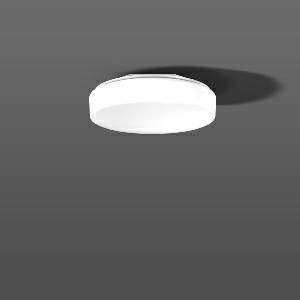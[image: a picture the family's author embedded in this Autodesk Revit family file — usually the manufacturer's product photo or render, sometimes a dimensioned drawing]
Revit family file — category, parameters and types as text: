
# Revit family: flat_polymero_kreis_672092_002_6_1_e46d
name_source: partatom
category: Lighting Fixtures
units: mm (PartAtom-declared; Revit-internal decimal feet)

## family parameters
Cut with Voids When Loaded = No
Host = Face
Light Source = No
Part Type = Normal
Room Calculation Point = No
Round Connector Dimension = Use Diameter
Shared = No

## types (1)
- FLAT POLYMERO KREIS (1 x LED Modul 840, 1800 lm, 4000)
    Apparent Load = 15 VA
    CIE Flux Codes = 43 73 91 87 100
    Color Rendering = 80
    Color Temperature = 4000
    Default Elevation = 1800 mm  [stored 5.90551 ft]
    Description = Series: FLAT POLYMERO KREIS
Decorative round surface-mounted luminaire. For escape route illumination. Base: metal, powder-coated. Diffuser made of plastic (polycarbonate), opal, shockproof. Diffuser fastening: patented push system. Suitable for Ceiling mounting, Wall (surface). Betriebsgeräte integriert. Einzelbatteriesystem mit automatischem Selbsttest. 
Colour: white
Diameter: 360 mm
Height: 109 mm
Weight: 1.87 kg
Operating mode: Combined NL readiness
Duration time: 3 h
Lamp: LED
Socket: without socket
Colour temperature: 4000K
Colour rendering index (CRI): 80
System power: 15 W
Rated luminous flux: 1800 lm
Luminous flux, emergency: 210 lm
System power, emergency: -
Control gear: Regulated power supply
Protection class: I
Type of protection: IP 40
    Height = 109 mm
    Lamp = 1 x LED Modul 840
    Lamp Light Flux = 1800 lm
    Lamp count = 1
    Length = 360 mm
    Lifetime = 50000 h
    Luminous efficacy = 120 lm/W
    Manufacturer = RZB
    ModVariant = No
    Model = 672092.002.6.1
    Mounting Place = Ceiling
    Mounting Type = Surface mounted
    Number of Poles = 1
    OnlyDefault = Yes
    Power Factor = 1
    Product Name = FLAT POLYMERO KREIS
    Product group = Surface mounted ceiling and wall luminaires
    ProductGroupID = 305
    Protection Class = Protection class I
    Protection Degree = Degree of protection
    RLX_Detail_Level = 1
    RLX_Emergency_Light_Flux = 210 lm
    RLX_Emergency_Type = 3
    RLX_Emergency_Type_DB = Yes
    RlxData = <blob elided: 52093 chars, md5=6eab48ec>
    Socket = socket
    Standby Power = 0 W
    System Light Flux = 1800 lm
    System Power = 15 W
    Type Comments = Product without accessories
    Type Image = 672092.002.1.jpg
    URL = http://relux.com
    VarID = ---
    Voltage = 0 V
    Weight = 0.00 kg
    Width = 0 mm  [stored 0 ft]

note: [stored X ft] marks values corroborated as IEEE doubles in the binary element streams (Revit-internal decimal feet)

## geometry (parser evidence)
native form markers: Blend x4, Sweep x12
no freeform markers — native parametric forms only
